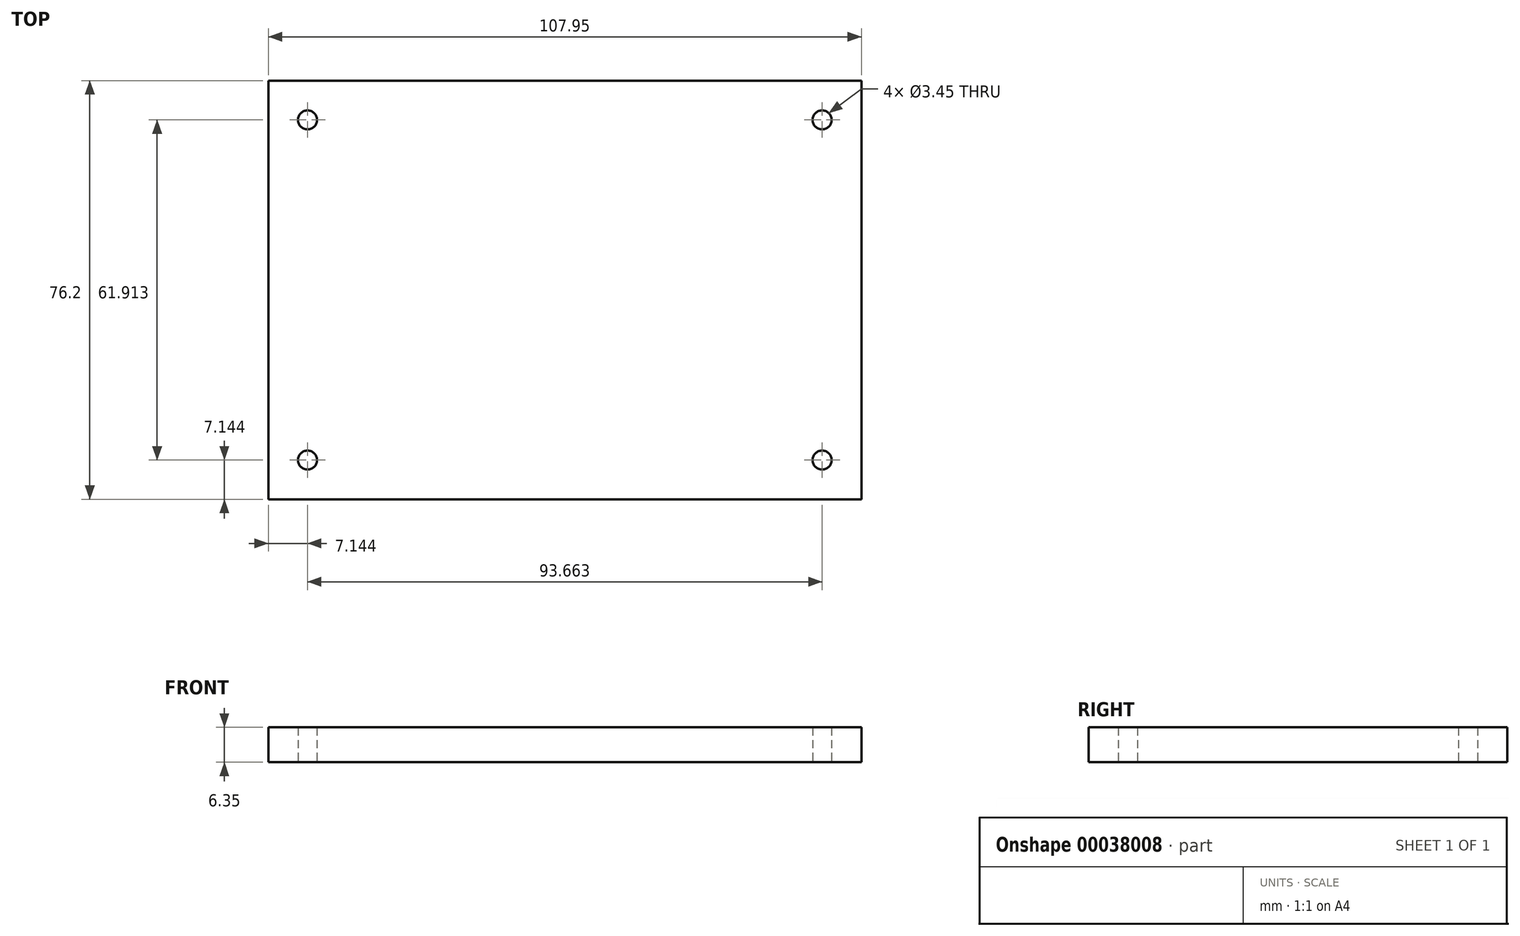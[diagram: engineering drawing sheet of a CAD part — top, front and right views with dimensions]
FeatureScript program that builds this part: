
annotation { "Feature Type Name" : "Feature", "Feature Type Description" : "" }
export const myFeature = defineFeature(function(context is Context, id is Id, definition is map)
    precondition{}
    {
        {
            var Q0;
            Q0=qCreatedBy(makeId("Top.planeOp"),FACE);
            var sketch = newSketch(context, id + "F0", { "sketchPlane" : qUnion([Q0])});
            skLineSegment(sketch, "E0.bottom", {"start": v(0, 0) * mm, "end": v(107.95, 0) * mm});
            skLineSegment(sketch, "E0.top", {"start": v(0, -76.2) * mm, "end": v(107.95, -76.2) * mm});
            skLineSegment(sketch, "E0.left", {"start": v(0, 0) * mm, "end": v(0, -76.2) * mm});
            skLineSegment(sketch, "E0.right", {"start": v(107.95, 0) * mm, "end": v(107.95, -76.2) * mm});
            skLineSegment(sketch, "E1", {"start": v(100.8, 0) * mm, "end": v(100.8, -7.14) * mm, "construction": true});
            skLineSegment(sketch, "E2", {"start": v(100.8, -7.14) * mm, "end": v(107.95, -7.14) * mm, "construction": true});
            skLineSegment(sketch, "E3", {"start": v(100.8, -76.2) * mm, "end": v(100.8, -69.06) * mm, "construction": true});
            skLineSegment(sketch, "E4", {"start": v(7.14, -76.2) * mm, "end": v(7.14, -69.06) * mm, "construction": true});
            skLineSegment(sketch, "E5", {"start": v(7.14, 0) * mm, "end": v(7.14, -7.14) * mm, "construction": true});
            skLineSegment(sketch, "E6", {"start": v(7.14, -7.14) * mm, "end": v(0, -7.14) * mm, "construction": true});
            skCircle(sketch, "E7", {"center": v(7.14, -7.14) * mm, "radius": 1.73 * mm});
            skCircle(sketch, "E8", {"center": v(100.8, -7.14) * mm, "radius": 1.73 * mm});
            skCircle(sketch, "E9", {"center": v(100.8, -69.06) * mm, "radius": 1.73 * mm});
            skCircle(sketch, "E10", {"center": v(7.14, -69.06) * mm, "radius": 1.73 * mm});
            skSolve(sketch);
        }
        {
            var Q0;
            Q0=qSketchRegion(id+"F0",true);
            extrude(context, id + "F1", {"entities" : qUnion([Q0]), "depth" : 6.35 * mm});
        }
    });
